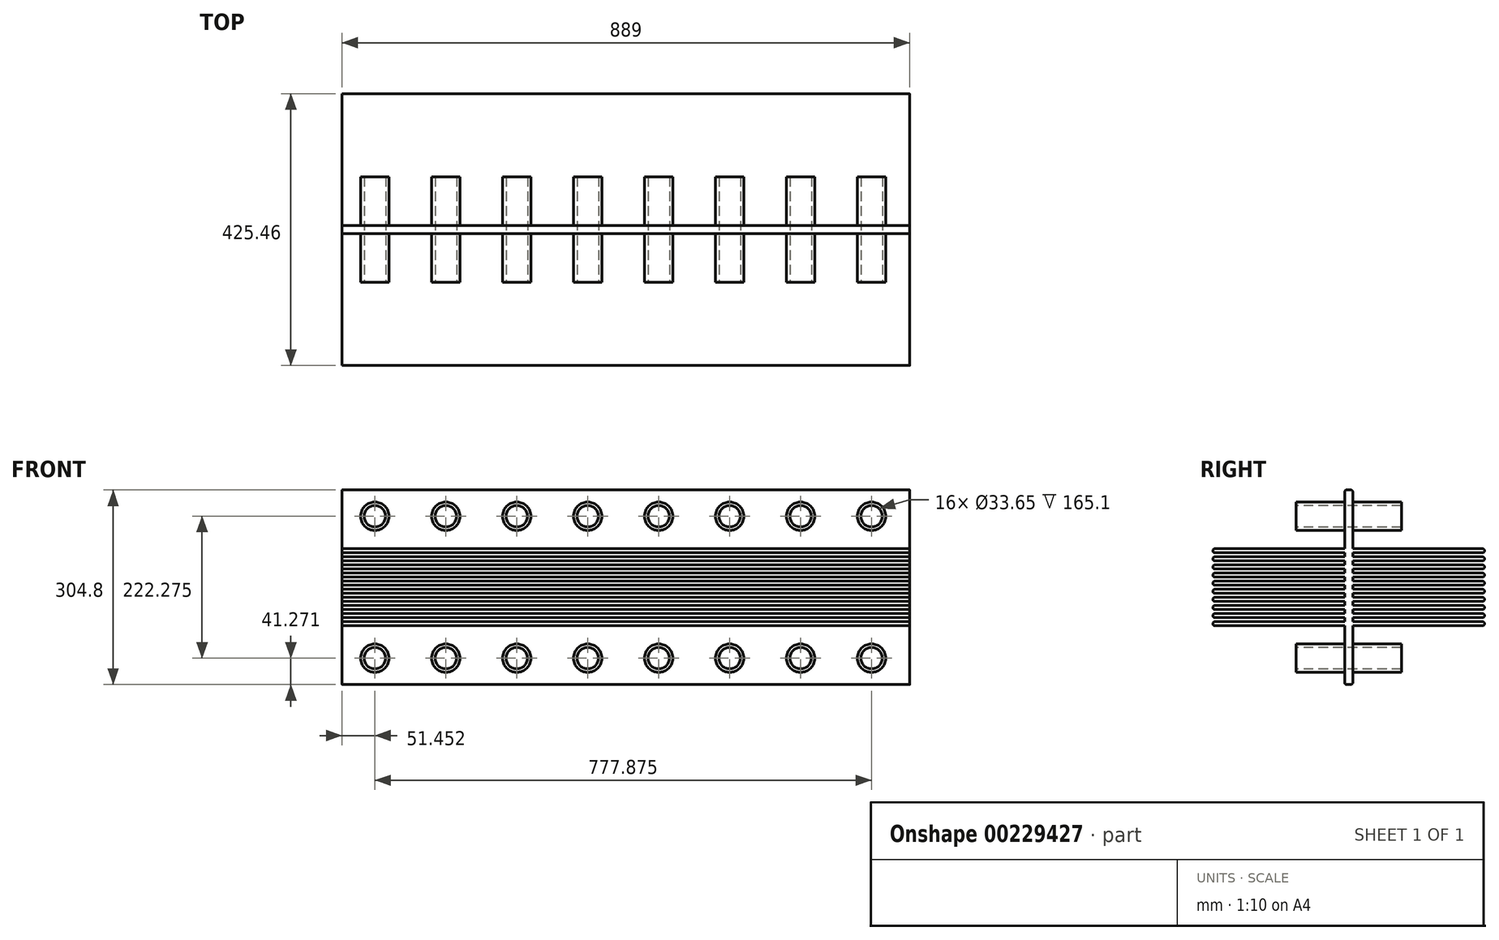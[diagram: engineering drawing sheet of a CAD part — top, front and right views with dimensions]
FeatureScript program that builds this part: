
annotation { "Feature Type Name" : "Feature", "Feature Type Description" : "" }
export const myFeature = defineFeature(function(context is Context, id is Id, definition is map)
    precondition{}
    {
        {
            var Q0;
            Q0=qCreatedBy(makeId("Front.planeOp"),FACE);
            var sketch = newSketch(context, id + "F0", { "sketchPlane" : qUnion([Q0])});
            skLineSegment(sketch, "E0.bottom", {"start": v(-439.22, 173.35) * mm, "end": v(449.78, 173.35) * mm});
            skLineSegment(sketch, "E0.top", {"start": v(-439.22, -131.45) * mm, "end": v(449.78, -131.45) * mm});
            skLineSegment(sketch, "E0.left", {"start": v(-439.22, 173.35) * mm, "end": v(-439.22, -131.45) * mm});
            skLineSegment(sketch, "E0.right", {"start": v(449.78, 173.35) * mm, "end": v(449.78, -131.45) * mm});
            skSolve(sketch);
        }
        {
            var Q0;
            Q0=makeQuery(id+"F0.imprint","IMPRINT",FACE,{"disambiguationData":[TD([[makeQuery(id+"F0.imprint","IMPRINT",EDGE,{"derivedFrom":sQuery(id+"F0.wireOp",EDGE,"E0.bottom")}),-1.0]])]});
            extrude(context, id + "F1", {"entities" : qUnion([Q0]), "depth" : 12.7 * mm});
        }
        {
            var Q0;
            Q0=makeQuery(id+"F1.opExtrude","CAP_FACE",FACE,{"disambiguationData":[OSD([sQuery(id+"F0.wireOp",EDGE,"E0.bottom"),sQuery(id+"F0.wireOp",EDGE,"E0.top"),sQuery(id+"F0.wireOp",EDGE,"E0.left"),sQuery(id+"F0.wireOp",EDGE,"E0.right")])],"isStart":false});
            var sketch = newSketch(context, id + "F2", { "sketchPlane" : qUnion([Q0])});
            skPoint(sketch, "E1", {"position": v(-387.77, -90.18) * mm});
            skPoint(sketch, "E2.0.1.0", {"position": v(-387.77, 132.1) * mm});
            skPoint(sketch, "E2.1.0.0", {"position": v(-276.64, -90.18) * mm});
            skPoint(sketch, "E2.1.1.0", {"position": v(-276.64, 132.1) * mm});
            skPoint(sketch, "E2.2.0.0", {"position": v(-165.52, -90.18) * mm});
            skPoint(sketch, "E2.2.1.0", {"position": v(-165.52, 132.1) * mm});
            skPoint(sketch, "E2.3.0.0", {"position": v(-54.4, -90.18) * mm});
            skPoint(sketch, "E2.3.1.0", {"position": v(-54.4, 132.1) * mm});
            skPoint(sketch, "E2.4.0.0", {"position": v(56.73, -90.18) * mm});
            skPoint(sketch, "E2.4.1.0", {"position": v(56.73, 132.1) * mm});
            skPoint(sketch, "E2.5.0.0", {"position": v(167.86, -90.18) * mm});
            skPoint(sketch, "E2.5.1.0", {"position": v(167.86, 132.1) * mm});
            skPoint(sketch, "E2.6.0.0", {"position": v(278.98, -90.18) * mm});
            skPoint(sketch, "E2.6.1.0", {"position": v(278.98, 132.1) * mm});
            skPoint(sketch, "E2.7.0.0", {"position": v(390.1, -90.18) * mm});
            skPoint(sketch, "E2.7.1.0", {"position": v(390.1, 132.1) * mm});
            skLineSegment(sketch, "E2.direction1", {"start": v(-387.77, -90.18) * mm, "end": v(-276.64, -90.18) * mm, "construction": true});
            skLineSegment(sketch, "E2.direction2", {"start": v(-387.77, -90.18) * mm, "end": v(-387.77, 132.1) * mm, "construction": true});
            skSolve(sketch);
        }
        {
            var Q0;
            Q0=makeQuery(id+"F1.opExtrude","SWEPT_FACE",FACE,{"disambiguationData":[OSD([sQuery(id+"F0.wireOp",EDGE,"E0.left")])]});
            var sketch = newSketch(context, id + "F3", { "sketchPlane" : qUnion([Q0])});
            skLineSegment(sketch, "E3", {"start": v(6.35, 173.35) * mm, "end": v(6.35, -131.45) * mm, "construction": true});
            skLineSegment(sketch, "E4", {"start": v(0, 20.95) * mm, "end": v(-70.4, 20.95) * mm, "construction": true});
            skPoint(sketch, "E4.endSnap0", {"position": v(0, 20.95) * mm});
            skLineSegment(sketch, "E5.MirrorCS", {"start": v(0, 24.12) * mm, "end": v(-203.2, 24.12) * mm});
            skLineSegment(sketch, "E6", {"start": v(0, 30.47) * mm, "end": v(-203.2, 30.47) * mm});
            skLineSegment(sketch, "E7", {"start": v(-203.2, 36.82) * mm, "end": v(0, 36.82) * mm});
            skLineSegment(sketch, "E8", {"start": v(-203.2, 43.17) * mm, "end": v(0, 43.17) * mm});
            skLineSegment(sketch, "E9", {"start": v(-203.2, 49.52) * mm, "end": v(0, 49.52) * mm});
            skLineSegment(sketch, "E10", {"start": v(-203.2, 55.87) * mm, "end": v(0, 55.87) * mm});
            skLineSegment(sketch, "E11", {"start": v(-203.2, 62.22) * mm, "end": v(0, 62.22) * mm});
            skLineSegment(sketch, "E12", {"start": v(-203.2, 68.57) * mm, "end": v(0, 68.57) * mm});
            skLineSegment(sketch, "E13", {"start": v(-203.2, 74.92) * mm, "end": v(0, 74.92) * mm});
            skLineSegment(sketch, "E14", {"start": v(-203.2, 81.27) * mm, "end": v(0, 81.27) * mm});
            skLineSegment(sketch, "E15.MirrorCS", {"start": v(12.7, 24.12) * mm, "end": v(215.9, 24.12) * mm});
            skLineSegment(sketch, "E16.MirrorCS", {"start": v(12.7, 30.47) * mm, "end": v(215.9, 30.47) * mm});
            skLineSegment(sketch, "E17.MirrorCS", {"start": v(215.9, 36.82) * mm, "end": v(12.7, 36.82) * mm});
            skLineSegment(sketch, "E18.MirrorCS", {"start": v(215.9, 43.17) * mm, "end": v(12.7, 43.17) * mm});
            skLineSegment(sketch, "E19.MirrorCS", {"start": v(215.9, 49.52) * mm, "end": v(12.7, 49.52) * mm});
            skLineSegment(sketch, "E20.MirrorCS", {"start": v(215.9, 55.87) * mm, "end": v(12.7, 55.87) * mm});
            skLineSegment(sketch, "E21.MirrorCS", {"start": v(215.9, 62.22) * mm, "end": v(12.7, 62.22) * mm});
            skLineSegment(sketch, "E22.MirrorCS", {"start": v(215.9, 68.57) * mm, "end": v(12.7, 68.57) * mm});
            skLineSegment(sketch, "E23.MirrorCS", {"start": v(215.9, 74.92) * mm, "end": v(12.7, 74.92) * mm});
            skLineSegment(sketch, "E24.MirrorCS", {"start": v(215.9, 81.27) * mm, "end": v(12.7, 81.27) * mm});
            skLineSegment(sketch, "E25.MirrorCS", {"start": v(0, 17.77) * mm, "end": v(-203.2, 17.77) * mm});
            skLineSegment(sketch, "E26.MirrorCS", {"start": v(0, 11.42) * mm, "end": v(-203.2, 11.42) * mm});
            skLineSegment(sketch, "E27.MirrorCS", {"start": v(-203.2, 5.07) * mm, "end": v(0, 5.07) * mm});
            skLineSegment(sketch, "E28.MirrorCS", {"start": v(-203.2, -1.28) * mm, "end": v(0, -1.28) * mm});
            skLineSegment(sketch, "E29.MirrorCS", {"start": v(-203.2, -7.63) * mm, "end": v(0, -7.63) * mm});
            skLineSegment(sketch, "E30.MirrorCS", {"start": v(-203.2, -13.98) * mm, "end": v(0, -13.98) * mm});
            skLineSegment(sketch, "E31.MirrorCS", {"start": v(-203.2, -20.33) * mm, "end": v(0, -20.33) * mm});
            skLineSegment(sketch, "E32.MirrorCS", {"start": v(-203.2, -26.68) * mm, "end": v(0, -26.68) * mm});
            skLineSegment(sketch, "E33.MirrorCS", {"start": v(-203.2, -33.03) * mm, "end": v(0, -33.03) * mm});
            skLineSegment(sketch, "E34.MirrorCS", {"start": v(-203.2, -39.38) * mm, "end": v(0, -39.38) * mm});
            skLineSegment(sketch, "E35.MirrorCS", {"start": v(215.9, -39.38) * mm, "end": v(12.7, -39.38) * mm});
            skLineSegment(sketch, "E36.MirrorCS", {"start": v(215.9, -33.03) * mm, "end": v(12.7, -33.03) * mm});
            skLineSegment(sketch, "E37.MirrorCS", {"start": v(215.9, -26.68) * mm, "end": v(12.7, -26.68) * mm});
            skLineSegment(sketch, "E38.MirrorCS", {"start": v(215.9, -20.33) * mm, "end": v(12.7, -20.33) * mm});
            skLineSegment(sketch, "E39.MirrorCS", {"start": v(215.9, -13.98) * mm, "end": v(12.7, -13.98) * mm});
            skLineSegment(sketch, "E40.MirrorCS", {"start": v(215.9, -7.63) * mm, "end": v(12.7, -7.63) * mm});
            skLineSegment(sketch, "E41.MirrorCS", {"start": v(215.9, -1.28) * mm, "end": v(12.7, -1.28) * mm});
            skLineSegment(sketch, "E42.MirrorCS", {"start": v(215.9, 5.07) * mm, "end": v(12.7, 5.07) * mm});
            skLineSegment(sketch, "E43.MirrorCS", {"start": v(12.7, 11.42) * mm, "end": v(215.9, 11.42) * mm});
            skLineSegment(sketch, "E44.MirrorCS", {"start": v(12.7, 17.77) * mm, "end": v(215.9, 17.77) * mm});
            skArc(sketch, "E45", {"start": v(-203.2, -33.03) * mm, "mid": v(-206.38, -36.2) * mm, "end": v(-203.2, -39.38) * mm});
            skArc(sketch, "E46", {"start": v(-203.2, -20.33) * mm, "mid": v(-206.37, -23.5) * mm, "end": v(-203.2, -26.68) * mm});
            skArc(sketch, "E47", {"start": v(-203.2, -7.63) * mm, "mid": v(-206.38, -10.8) * mm, "end": v(-203.2, -13.98) * mm});
            skArc(sketch, "E48", {"start": v(-203.2, 5.07) * mm, "mid": v(-206.38, 1.9) * mm, "end": v(-203.2, -1.28) * mm});
            skArc(sketch, "E49", {"start": v(-203.2, 17.77) * mm, "mid": v(-206.38, 14.6) * mm, "end": v(-203.2, 11.42) * mm});
            skArc(sketch, "E50", {"start": v(-203.2, 30.47) * mm, "mid": v(-206.38, 27.3) * mm, "end": v(-203.2, 24.12) * mm});
            skArc(sketch, "E51", {"start": v(-203.2, 43.17) * mm, "mid": v(-206.38, 40) * mm, "end": v(-203.2, 36.82) * mm});
            skArc(sketch, "E52", {"start": v(-203.2, 55.87) * mm, "mid": v(-206.38, 52.7) * mm, "end": v(-203.2, 49.52) * mm});
            skArc(sketch, "E53", {"start": v(-203.2, 68.57) * mm, "mid": v(-206.38, 65.4) * mm, "end": v(-203.2, 62.22) * mm});
            skArc(sketch, "E54", {"start": v(-203.2, 81.27) * mm, "mid": v(-206.38, 78.1) * mm, "end": v(-203.2, 74.92) * mm});
            skArc(sketch, "E55.MirrorCS", {"start": v(215.9, 81.27) * mm, "mid": v(219.08, 78.1) * mm, "end": v(215.9, 74.92) * mm});
            skArc(sketch, "E56.MirrorCS", {"start": v(215.9, 68.57) * mm, "mid": v(219.08, 65.4) * mm, "end": v(215.9, 62.22) * mm});
            skArc(sketch, "E57.MirrorCS", {"start": v(215.9, 55.87) * mm, "mid": v(219.08, 52.7) * mm, "end": v(215.9, 49.52) * mm});
            skArc(sketch, "E58.MirrorCS", {"start": v(215.9, 43.17) * mm, "mid": v(219.08, 40) * mm, "end": v(215.9, 36.82) * mm});
            skArc(sketch, "E59.MirrorCS", {"start": v(215.9, 30.47) * mm, "mid": v(219.08, 27.3) * mm, "end": v(215.9, 24.12) * mm});
            skArc(sketch, "E60.MirrorCS", {"start": v(215.9, 17.77) * mm, "mid": v(219.08, 14.6) * mm, "end": v(215.9, 11.42) * mm});
            skArc(sketch, "E61.MirrorCS", {"start": v(215.9, 5.07) * mm, "mid": v(219.08, 1.9) * mm, "end": v(215.9, -1.28) * mm});
            skArc(sketch, "E62.MirrorCS", {"start": v(215.9, -7.63) * mm, "mid": v(219.08, -10.8) * mm, "end": v(215.9, -13.98) * mm});
            skArc(sketch, "E63.MirrorCS", {"start": v(215.9, -20.33) * mm, "mid": v(219.07, -23.5) * mm, "end": v(215.9, -26.68) * mm});
            skArc(sketch, "E64.MirrorCS", {"start": v(215.9, -33.03) * mm, "mid": v(219.08, -36.2) * mm, "end": v(215.9, -39.38) * mm});
            skLineSegment(sketch, "E65", {"start": v(0, 81.27) * mm, "end": v(6.35, 81.27) * mm});
            skLineSegment(sketch, "E66", {"start": v(6.35, 81.27) * mm, "end": v(12.7, 81.27) * mm});
            skLineSegment(sketch, "E67", {"start": v(0, -39.38) * mm, "end": v(6.35, -39.38) * mm});
            skLineSegment(sketch, "E68", {"start": v(6.35, -39.38) * mm, "end": v(12.7, -39.38) * mm});
            skSolve(sketch);
        }
        {
            var Q0;
            Q0=makeQuery(id+"F1.opExtrude","SWEPT_FACE",FACE,{"disambiguationData":[OSD([sQuery(id+"F0.wireOp",EDGE,"E0.left")])]});
            var Q1;
            {var subQ0=sQuery(id+"F3.wireOp",EDGE,"E33.MirrorCS");Q1=makeQuery(id+"F3.imprint","IMPRINT",FACE,{"disambiguationData":[TD([[makeQuery(id+"F3.imprint","IMPRINT",EDGE,{"derivedFrom":subQ0}),-1.0]])]});}
            var Q2;
            {var subQ0=sQuery(id+"F3.wireOp",EDGE,"E31.MirrorCS");Q2=makeQuery(id+"F3.imprint","IMPRINT",FACE,{"disambiguationData":[TD([[makeQuery(id+"F3.imprint","IMPRINT",EDGE,{"derivedFrom":subQ0}),-1.0]])]});}
            var Q3;
            {var subQ0=sQuery(id+"F3.wireOp",EDGE,"E29.MirrorCS");Q3=makeQuery(id+"F3.imprint","IMPRINT",FACE,{"disambiguationData":[TD([[makeQuery(id+"F3.imprint","IMPRINT",EDGE,{"derivedFrom":subQ0}),-1.0]])]});}
            var Q4;
            {var subQ0=sQuery(id+"F3.wireOp",EDGE,"E27.MirrorCS");Q4=makeQuery(id+"F3.imprint","IMPRINT",FACE,{"disambiguationData":[TD([[makeQuery(id+"F3.imprint","IMPRINT",EDGE,{"derivedFrom":subQ0}),-1.0]])]});}
            var Q5;
            {var subQ0=sQuery(id+"F3.wireOp",EDGE,"E25.MirrorCS");Q5=makeQuery(id+"F3.imprint","IMPRINT",FACE,{"disambiguationData":[TD([[makeQuery(id+"F3.imprint","IMPRINT",EDGE,{"derivedFrom":subQ0}),1.0]])]});}
            var Q6;
            {var subQ0=sQuery(id+"F3.wireOp",EDGE,"E5.MirrorCS");Q6=makeQuery(id+"F3.imprint","IMPRINT",FACE,{"disambiguationData":[TD([[makeQuery(id+"F3.imprint","IMPRINT",EDGE,{"derivedFrom":subQ0}),-1.0]])]});}
            var Q7;
            {var subQ0=sQuery(id+"F3.wireOp",EDGE,"E7");Q7=makeQuery(id+"F3.imprint","IMPRINT",FACE,{"disambiguationData":[TD([[makeQuery(id+"F3.imprint","IMPRINT",EDGE,{"derivedFrom":subQ0}),1.0]])]});}
            var Q8;
            {var subQ0=sQuery(id+"F3.wireOp",EDGE,"E9");Q8=makeQuery(id+"F3.imprint","IMPRINT",FACE,{"disambiguationData":[TD([[makeQuery(id+"F3.imprint","IMPRINT",EDGE,{"derivedFrom":subQ0}),1.0]])]});}
            var Q9;
            {var subQ0=sQuery(id+"F3.wireOp",EDGE,"E11");Q9=makeQuery(id+"F3.imprint","IMPRINT",FACE,{"disambiguationData":[TD([[makeQuery(id+"F3.imprint","IMPRINT",EDGE,{"derivedFrom":subQ0}),1.0]])]});}
            var Q10;
            {var subQ0=sQuery(id+"F3.wireOp",EDGE,"E13");Q10=makeQuery(id+"F3.imprint","IMPRINT",FACE,{"disambiguationData":[TD([[makeQuery(id+"F3.imprint","IMPRINT",EDGE,{"derivedFrom":subQ0}),1.0]])]});}
            var Q11;
            {var subQ0=sQuery(id+"F3.wireOp",EDGE,"E35.MirrorCS");Q11=makeQuery(id+"F3.imprint","IMPRINT",FACE,{"disambiguationData":[TD([[makeQuery(id+"F3.imprint","IMPRINT",EDGE,{"derivedFrom":subQ0}),-1.0]])]});}
            var Q12;
            {var subQ0=sQuery(id+"F3.wireOp",EDGE,"E37.MirrorCS");Q12=makeQuery(id+"F3.imprint","IMPRINT",FACE,{"disambiguationData":[TD([[makeQuery(id+"F3.imprint","IMPRINT",EDGE,{"derivedFrom":subQ0}),-1.0]])]});}
            var Q13;
            {var subQ0=sQuery(id+"F3.wireOp",EDGE,"E39.MirrorCS");Q13=makeQuery(id+"F3.imprint","IMPRINT",FACE,{"disambiguationData":[TD([[makeQuery(id+"F3.imprint","IMPRINT",EDGE,{"derivedFrom":subQ0}),-1.0]])]});}
            var Q14;
            {var subQ0=sQuery(id+"F3.wireOp",EDGE,"E41.MirrorCS");Q14=makeQuery(id+"F3.imprint","IMPRINT",FACE,{"disambiguationData":[TD([[makeQuery(id+"F3.imprint","IMPRINT",EDGE,{"derivedFrom":subQ0}),-1.0]])]});}
            var Q15;
            {var subQ0=sQuery(id+"F3.wireOp",EDGE,"E43.MirrorCS");Q15=makeQuery(id+"F3.imprint","IMPRINT",FACE,{"disambiguationData":[TD([[makeQuery(id+"F3.imprint","IMPRINT",EDGE,{"derivedFrom":subQ0}),1.0]])]});}
            var Q16;
            {var subQ0=sQuery(id+"F3.wireOp",EDGE,"E15.MirrorCS");Q16=makeQuery(id+"F3.imprint","IMPRINT",FACE,{"disambiguationData":[TD([[makeQuery(id+"F3.imprint","IMPRINT",EDGE,{"derivedFrom":subQ0}),1.0]])]});}
            var Q17;
            {var subQ0=sQuery(id+"F3.wireOp",EDGE,"E17.MirrorCS");Q17=makeQuery(id+"F3.imprint","IMPRINT",FACE,{"disambiguationData":[TD([[makeQuery(id+"F3.imprint","IMPRINT",EDGE,{"derivedFrom":subQ0}),-1.0]])]});}
            var Q18;
            {var subQ0=sQuery(id+"F3.wireOp",EDGE,"E19.MirrorCS");Q18=makeQuery(id+"F3.imprint","IMPRINT",FACE,{"disambiguationData":[TD([[makeQuery(id+"F3.imprint","IMPRINT",EDGE,{"derivedFrom":subQ0}),-1.0]])]});}
            var Q19;
            {var subQ0=sQuery(id+"F3.wireOp",EDGE,"E21.MirrorCS");Q19=makeQuery(id+"F3.imprint","IMPRINT",FACE,{"disambiguationData":[TD([[makeQuery(id+"F3.imprint","IMPRINT",EDGE,{"derivedFrom":subQ0}),-1.0]])]});}
            var Q20;
            {var subQ0=sQuery(id+"F3.wireOp",EDGE,"E23.MirrorCS");Q20=makeQuery(id+"F3.imprint","IMPRINT",FACE,{"disambiguationData":[TD([[makeQuery(id+"F3.imprint","IMPRINT",EDGE,{"derivedFrom":subQ0}),-1.0]])]});}
            var Q21;
            Q21=makeQuery(id+"F1.opExtrude","SWEPT_FACE",FACE,{"disambiguationData":[OSD([sQuery(id+"F0.wireOp",EDGE,"E0.right")])]});
            extrude(context, id + "F4", {"entities" : qUnion([Q0, Q1, Q2, Q3, Q4, Q5, Q6, Q7, Q8, Q9, Q10, Q11, Q12, Q13, Q14, Q15, Q16, Q17, Q18, Q19, Q20]), "operationType" : NewBodyOperationType.ADD, "endBound" : BoundingType.UP_TO_SURFACE, "oppositeDirection" : true, "endBoundEntityFace" : qUnion([Q21]), "depth" : 25.4 * mm});
        }
        {
            var Q0;
            Q0=makeQuery(id+"F1.opExtrude","CAP_EDGE",EDGE,{"disambiguationData":[OSD([sQuery(id+"F0.wireOp",EDGE,"E0.bottom")])],"isStart":false});
            var Q1;
            Q1=makeQuery(id+"F1.opExtrude","CAP_EDGE",EDGE,{"disambiguationData":[OSD([sQuery(id+"F0.wireOp",EDGE,"E0.bottom")])],"isStart":true});
            var Q2;
            Q2=makeQuery(id+"F1.opExtrude","CAP_EDGE",EDGE,{"disambiguationData":[OSD([sQuery(id+"F0.wireOp",EDGE,"E0.top")])],"isStart":false});
            var Q3;
            Q3=makeQuery(id+"F1.opExtrude","CAP_EDGE",EDGE,{"disambiguationData":[OSD([sQuery(id+"F0.wireOp",EDGE,"E0.top")])],"isStart":true});
            fillet(context, id + "F5", {"entities" : qUnion([Q0, Q1, Q2, Q3]), "radius" : 3.17 * mm, "tangentPropagation" : true, "allowEdgeOverflow" : false});
        }
        {
            var Q0;
            Q0=sQuery(id+"F2.wireOp",VERTEX,"E1");
            var Q1;
            Q1=sQuery(id+"F2.wireOp",VERTEX,"E2.1.0.0");
            var Q2;
            Q2=sQuery(id+"F2.wireOp",VERTEX,"E2.2.0.0");
            var Q3;
            Q3=sQuery(id+"F2.wireOp",VERTEX,"E2.3.0.0");
            var Q4;
            Q4=sQuery(id+"F2.wireOp",VERTEX,"E2.4.0.0");
            var Q5;
            Q5=sQuery(id+"F2.wireOp",VERTEX,"E2.5.0.0");
            var Q6;
            Q6=sQuery(id+"F2.wireOp",VERTEX,"E2.6.0.0");
            var Q7;
            Q7=sQuery(id+"F2.wireOp",VERTEX,"E2.5.1.0");
            var Q8;
            Q8=sQuery(id+"F2.wireOp",VERTEX,"E2.4.1.0");
            var Q9;
            Q9=sQuery(id+"F2.wireOp",VERTEX,"E2.3.1.0");
            var Q10;
            Q10=sQuery(id+"F2.wireOp",VERTEX,"E2.2.1.0");
            var Q11;
            Q11=sQuery(id+"F2.wireOp",VERTEX,"E2.1.1.0");
            var Q12;
            Q12=sQuery(id+"F2.wireOp",VERTEX,"E2.0.1.0");
            var Q13;
            Q13=sQuery(id+"F2.wireOp",VERTEX,"E2.7.0.0");
            var Q14;
            Q14=sQuery(id+"F2.wireOp",VERTEX,"E2.7.1.0");
            var Q15;
            Q15=sQuery(id+"F2.wireOp",VERTEX,"E2.6.1.0");
            var Q16;
            Q16=makeQuery(id+"F1.opExtrude","SWEPT_BODY",BODY,{"disambiguationData":[OSD([sQuery(id+"F0.wireOp",EDGE,"E0.bottom"),sQuery(id+"F0.wireOp",EDGE,"E0.top"),sQuery(id+"F0.wireOp",EDGE,"E0.left"),sQuery(id+"F0.wireOp",EDGE,"E0.right")])]});
            hole(context, id + "F6", {"style" : HoleStyle.SIMPLE, "endStyle" : HoleEndStyle.THROUGH, "holeDiameter" : 33.65 * mm, "locations" : qUnion([Q0, Q1, Q2, Q3, Q4, Q5, Q6, Q7, Q8, Q9, Q10, Q11, Q12, Q13, Q14, Q15]), "scope" : qUnion([Q16]), "isTappedThrough" : true});
        }
        {
            var Q0;
            {var subQ3=sQuery(id+"F0.wireOp",EDGE,"E0.left");var subQ16=sQuery(id+"F0.wireOp",EDGE,"E0.right");var subQ44=sQuery(id+"F0.wireOp",EDGE,"E0.top");Q0=makeQuery(id+"F4.boolean.opBoolean","SPLIT",FACE,{"disambiguationData":[TD([makeQuery(id+"F1.opExtrude","SWEPT_FACE",FACE,{"disambiguationData":[OSD([subQ44])]})])],"derivedFrom":makeQuery(id+"F1.opExtrude","CAP_FACE",FACE,{"disambiguationData":[OSD([sQuery(id+"F0.wireOp",EDGE,"E0.bottom"),subQ44,subQ3,subQ16])],"isStart":false})});}
            var sketch = newSketch(context, id + "F7", { "sketchPlane" : qUnion([Q0])});
            skCircle(sketch, "E69", {"center": v(-387.77, -90.18) * mm, "radius": 22.24 * mm});
            skCircle(sketch, "E70.1.0.0", {"center": v(-276.64, -90.18) * mm, "radius": 22.24 * mm});
            skCircle(sketch, "E70.2.0.0", {"center": v(-165.52, -90.18) * mm, "radius": 22.24 * mm});
            skCircle(sketch, "E70.3.0.0", {"center": v(-54.4, -90.18) * mm, "radius": 22.24 * mm});
            skCircle(sketch, "E70.4.0.0", {"center": v(56.73, -90.18) * mm, "radius": 22.24 * mm});
            skCircle(sketch, "E70.5.0.0", {"center": v(167.86, -90.18) * mm, "radius": 22.24 * mm});
            skCircle(sketch, "E70.6.0.0", {"center": v(278.98, -90.18) * mm, "radius": 22.24 * mm});
            skCircle(sketch, "E70.7.0.0", {"center": v(390.1, -90.18) * mm, "radius": 22.24 * mm});
            skLineSegment(sketch, "E70.direction1", {"start": v(-387.77, -90.18) * mm, "end": v(-276.64, -90.18) * mm, "construction": true});
            skSolve(sketch);
        }
        {
            var Q0;
            {var subQ3=sQuery(id+"F0.wireOp",EDGE,"E0.left");var subQ13=sQuery(id+"F0.wireOp",EDGE,"E0.right");var subQ44=sQuery(id+"F0.wireOp",EDGE,"E0.bottom");Q0=makeQuery(id+"F4.boolean.opBoolean","SPLIT",FACE,{"disambiguationData":[TD([makeQuery(id+"F1.opExtrude","SWEPT_FACE",FACE,{"disambiguationData":[OSD([subQ44])]})])],"derivedFrom":makeQuery(id+"F1.opExtrude","CAP_FACE",FACE,{"disambiguationData":[OSD([subQ44,sQuery(id+"F0.wireOp",EDGE,"E0.top"),subQ3,subQ13])],"isStart":false})});}
            var sketch = newSketch(context, id + "F8", { "sketchPlane" : qUnion([Q0])});
            skCircle(sketch, "E71", {"center": v(-387.77, 132.1) * mm, "radius": 22.24 * mm});
            skCircle(sketch, "E72.1.0.0", {"center": v(-276.64, 132.1) * mm, "radius": 22.24 * mm});
            skCircle(sketch, "E72.2.0.0", {"center": v(-165.52, 132.1) * mm, "radius": 22.24 * mm});
            skCircle(sketch, "E72.3.0.0", {"center": v(-54.4, 132.1) * mm, "radius": 22.24 * mm});
            skCircle(sketch, "E72.4.0.0", {"center": v(56.73, 132.1) * mm, "radius": 22.24 * mm});
            skCircle(sketch, "E72.5.0.0", {"center": v(167.86, 132.1) * mm, "radius": 22.24 * mm});
            skCircle(sketch, "E72.6.0.0", {"center": v(278.98, 132.1) * mm, "radius": 22.24 * mm});
            skCircle(sketch, "E72.7.0.0", {"center": v(390.1, 132.1) * mm, "radius": 22.24 * mm});
            skLineSegment(sketch, "E72.direction1", {"start": v(-387.77, 132.1) * mm, "end": v(-276.64, 132.1) * mm, "construction": true});
            skSolve(sketch);
        }
        {
            var Q0;
            Q0=makeQuery(id+"F8.imprint","IMPRINT",FACE,{"disambiguationData":[TD([[makeQuery(id+"F8.imprint","IMPRINT",EDGE,{"derivedFrom":sQuery(id+"F8.wireOp",EDGE,"E71")}),1.0]])]});
            var Q1;
            Q1=makeQuery(id+"F8.imprint","IMPRINT",FACE,{"disambiguationData":[TD([[makeQuery(id+"F8.imprint","IMPRINT",EDGE,{"derivedFrom":sQuery(id+"F8.wireOp",EDGE,"E72.1.0.0")}),1.0]])]});
            var Q2;
            Q2=makeQuery(id+"F8.imprint","IMPRINT",FACE,{"disambiguationData":[TD([[makeQuery(id+"F8.imprint","IMPRINT",EDGE,{"derivedFrom":sQuery(id+"F8.wireOp",EDGE,"E72.2.0.0")}),1.0]])]});
            var Q3;
            Q3=makeQuery(id+"F8.imprint","IMPRINT",FACE,{"disambiguationData":[TD([[makeQuery(id+"F8.imprint","IMPRINT",EDGE,{"derivedFrom":sQuery(id+"F8.wireOp",EDGE,"E72.3.0.0")}),1.0]])]});
            var Q4;
            Q4=makeQuery(id+"F8.imprint","IMPRINT",FACE,{"disambiguationData":[TD([[makeQuery(id+"F8.imprint","IMPRINT",EDGE,{"derivedFrom":sQuery(id+"F8.wireOp",EDGE,"E72.4.0.0")}),1.0]])]});
            var Q5;
            Q5=makeQuery(id+"F8.imprint","IMPRINT",FACE,{"disambiguationData":[TD([[makeQuery(id+"F8.imprint","IMPRINT",EDGE,{"derivedFrom":sQuery(id+"F8.wireOp",EDGE,"E72.5.0.0")}),1.0]])]});
            var Q6;
            Q6=makeQuery(id+"F8.imprint","IMPRINT",FACE,{"disambiguationData":[TD([[makeQuery(id+"F8.imprint","IMPRINT",EDGE,{"derivedFrom":sQuery(id+"F8.wireOp",EDGE,"E72.6.0.0")}),1.0]])]});
            var Q7;
            Q7=makeQuery(id+"F8.imprint","IMPRINT",FACE,{"disambiguationData":[TD([[makeQuery(id+"F8.imprint","IMPRINT",EDGE,{"derivedFrom":sQuery(id+"F8.wireOp",EDGE,"E72.7.0.0")}),1.0]])]});
            var Q8;
            Q8=makeQuery(id+"F7.imprint","IMPRINT",FACE,{"disambiguationData":[TD([[makeQuery(id+"F7.imprint","IMPRINT",EDGE,{"derivedFrom":sQuery(id+"F7.wireOp",EDGE,"E69")}),1.0]])]});
            var Q9;
            Q9=makeQuery(id+"F7.imprint","IMPRINT",FACE,{"disambiguationData":[TD([[makeQuery(id+"F7.imprint","IMPRINT",EDGE,{"derivedFrom":sQuery(id+"F7.wireOp",EDGE,"E70.1.0.0")}),1.0]])]});
            var Q10;
            Q10=makeQuery(id+"F7.imprint","IMPRINT",FACE,{"disambiguationData":[TD([[makeQuery(id+"F7.imprint","IMPRINT",EDGE,{"derivedFrom":sQuery(id+"F7.wireOp",EDGE,"E70.2.0.0")}),1.0]])]});
            var Q11;
            Q11=makeQuery(id+"F7.imprint","IMPRINT",FACE,{"disambiguationData":[TD([[makeQuery(id+"F7.imprint","IMPRINT",EDGE,{"derivedFrom":sQuery(id+"F7.wireOp",EDGE,"E70.3.0.0")}),1.0]])]});
            var Q12;
            Q12=makeQuery(id+"F7.imprint","IMPRINT",FACE,{"disambiguationData":[TD([[makeQuery(id+"F7.imprint","IMPRINT",EDGE,{"derivedFrom":sQuery(id+"F7.wireOp",EDGE,"E70.4.0.0")}),1.0]])]});
            var Q13;
            Q13=makeQuery(id+"F7.imprint","IMPRINT",FACE,{"disambiguationData":[TD([[makeQuery(id+"F7.imprint","IMPRINT",EDGE,{"derivedFrom":sQuery(id+"F7.wireOp",EDGE,"E70.5.0.0")}),1.0]])]});
            var Q14;
            Q14=makeQuery(id+"F7.imprint","IMPRINT",FACE,{"disambiguationData":[TD([[makeQuery(id+"F7.imprint","IMPRINT",EDGE,{"derivedFrom":sQuery(id+"F7.wireOp",EDGE,"E70.6.0.0")}),1.0]])]});
            var Q15;
            Q15=makeQuery(id+"F7.imprint","IMPRINT",FACE,{"disambiguationData":[TD([[makeQuery(id+"F7.imprint","IMPRINT",EDGE,{"derivedFrom":sQuery(id+"F7.wireOp",EDGE,"E70.7.0.0")}),1.0]])]});
            extrude(context, id + "F9", {"entities" : qUnion([Q0, Q1, Q2, Q3, Q4, Q5, Q6, Q7, Q8, Q9, Q10, Q11, Q12, Q13, Q14, Q15]), "operationType" : NewBodyOperationType.ADD, "depth" : 76.2 * mm});
        }
        {
            var Q0;
            {var subQ3=sQuery(id+"F0.wireOp",EDGE,"E0.left");var subQ13=sQuery(id+"F0.wireOp",EDGE,"E0.right");var subQ44=sQuery(id+"F0.wireOp",EDGE,"E0.bottom");Q0=makeQuery(id+"F4.boolean.opBoolean","SPLIT",FACE,{"disambiguationData":[TD([makeQuery(id+"F1.opExtrude","SWEPT_FACE",FACE,{"disambiguationData":[OSD([subQ44])]})])],"derivedFrom":makeQuery(id+"F1.opExtrude","CAP_FACE",FACE,{"disambiguationData":[OSD([subQ44,sQuery(id+"F0.wireOp",EDGE,"E0.top"),subQ3,subQ13])],"isStart":true})});}
            var sketch = newSketch(context, id + "F10", { "sketchPlane" : qUnion([Q0])});
            skCircle(sketch, "E73", {"center": v(-390.1, 132.1) * mm, "radius": 22.24 * mm});
            skCircle(sketch, "E74.1.0.0", {"center": v(-278.98, 132.1) * mm, "radius": 22.24 * mm});
            skCircle(sketch, "E74.2.0.0", {"center": v(-167.86, 132.1) * mm, "radius": 22.24 * mm});
            skCircle(sketch, "E74.3.0.0", {"center": v(-56.73, 132.1) * mm, "radius": 22.24 * mm});
            skCircle(sketch, "E74.4.0.0", {"center": v(54.4, 132.1) * mm, "radius": 22.24 * mm});
            skCircle(sketch, "E74.5.0.0", {"center": v(165.52, 132.1) * mm, "radius": 22.24 * mm});
            skCircle(sketch, "E74.6.0.0", {"center": v(276.64, 132.1) * mm, "radius": 22.24 * mm});
            skCircle(sketch, "E74.7.0.0", {"center": v(387.77, 132.1) * mm, "radius": 22.24 * mm});
            skLineSegment(sketch, "E74.direction1", {"start": v(-390.1, 132.1) * mm, "end": v(-278.98, 132.1) * mm, "construction": true});
            skSolve(sketch);
        }
        {
            var Q0;
            {var subQ3=sQuery(id+"F0.wireOp",EDGE,"E0.left");var subQ10=sQuery(id+"F0.wireOp",EDGE,"E0.right");var subQ44=sQuery(id+"F0.wireOp",EDGE,"E0.top");Q0=makeQuery(id+"F4.boolean.opBoolean","SPLIT",FACE,{"disambiguationData":[TD([makeQuery(id+"F1.opExtrude","SWEPT_FACE",FACE,{"disambiguationData":[OSD([subQ44])]})])],"derivedFrom":makeQuery(id+"F1.opExtrude","CAP_FACE",FACE,{"disambiguationData":[OSD([sQuery(id+"F0.wireOp",EDGE,"E0.bottom"),subQ44,subQ3,subQ10])],"isStart":true})});}
            var sketch = newSketch(context, id + "F11", { "sketchPlane" : qUnion([Q0])});
            skCircle(sketch, "E75", {"center": v(-390.1, -90.18) * mm, "radius": 22.24 * mm});
            skCircle(sketch, "E76.1.0.0", {"center": v(-278.98, -90.18) * mm, "radius": 22.24 * mm});
            skCircle(sketch, "E76.2.0.0", {"center": v(-167.86, -90.18) * mm, "radius": 22.24 * mm});
            skCircle(sketch, "E76.3.0.0", {"center": v(-56.73, -90.18) * mm, "radius": 22.24 * mm});
            skCircle(sketch, "E76.4.0.0", {"center": v(54.4, -90.18) * mm, "radius": 22.24 * mm});
            skCircle(sketch, "E76.5.0.0", {"center": v(165.52, -90.18) * mm, "radius": 22.24 * mm});
            skCircle(sketch, "E76.6.0.0", {"center": v(276.64, -90.18) * mm, "radius": 22.24 * mm});
            skCircle(sketch, "E76.7.0.0", {"center": v(387.77, -90.18) * mm, "radius": 22.24 * mm});
            skLineSegment(sketch, "E76.direction1", {"start": v(-390.1, -90.18) * mm, "end": v(-278.98, -90.18) * mm, "construction": true});
            skSolve(sketch);
        }
        {
            var Q0;
            Q0=makeQuery(id+"F10.imprint","IMPRINT",FACE,{"disambiguationData":[TD([[makeQuery(id+"F10.imprint","IMPRINT",EDGE,{"derivedFrom":sQuery(id+"F10.wireOp",EDGE,"E73")}),1.0]])]});
            var Q1;
            Q1=makeQuery(id+"F10.imprint","IMPRINT",FACE,{"disambiguationData":[TD([[makeQuery(id+"F10.imprint","IMPRINT",EDGE,{"derivedFrom":sQuery(id+"F10.wireOp",EDGE,"E74.1.0.0")}),1.0]])]});
            var Q2;
            Q2=makeQuery(id+"F10.imprint","IMPRINT",FACE,{"disambiguationData":[TD([[makeQuery(id+"F10.imprint","IMPRINT",EDGE,{"derivedFrom":sQuery(id+"F10.wireOp",EDGE,"E74.2.0.0")}),1.0]])]});
            var Q3;
            Q3=makeQuery(id+"F10.imprint","IMPRINT",FACE,{"disambiguationData":[TD([[makeQuery(id+"F10.imprint","IMPRINT",EDGE,{"derivedFrom":sQuery(id+"F10.wireOp",EDGE,"E74.3.0.0")}),1.0]])]});
            var Q4;
            Q4=makeQuery(id+"F10.imprint","IMPRINT",FACE,{"disambiguationData":[TD([[makeQuery(id+"F10.imprint","IMPRINT",EDGE,{"derivedFrom":sQuery(id+"F10.wireOp",EDGE,"E74.4.0.0")}),1.0]])]});
            var Q5;
            Q5=makeQuery(id+"F10.imprint","IMPRINT",FACE,{"disambiguationData":[TD([[makeQuery(id+"F10.imprint","IMPRINT",EDGE,{"derivedFrom":sQuery(id+"F10.wireOp",EDGE,"E74.5.0.0")}),1.0]])]});
            var Q6;
            Q6=makeQuery(id+"F10.imprint","IMPRINT",FACE,{"disambiguationData":[TD([[makeQuery(id+"F10.imprint","IMPRINT",EDGE,{"derivedFrom":sQuery(id+"F10.wireOp",EDGE,"E74.6.0.0")}),1.0]])]});
            var Q7;
            Q7=makeQuery(id+"F10.imprint","IMPRINT",FACE,{"disambiguationData":[TD([[makeQuery(id+"F10.imprint","IMPRINT",EDGE,{"derivedFrom":sQuery(id+"F10.wireOp",EDGE,"E74.7.0.0")}),1.0]])]});
            var Q8;
            Q8=makeQuery(id+"F11.imprint","IMPRINT",FACE,{"disambiguationData":[TD([[makeQuery(id+"F11.imprint","IMPRINT",EDGE,{"derivedFrom":sQuery(id+"F11.wireOp",EDGE,"E75")}),1.0]])]});
            var Q9;
            Q9=makeQuery(id+"F11.imprint","IMPRINT",FACE,{"disambiguationData":[TD([[makeQuery(id+"F11.imprint","IMPRINT",EDGE,{"derivedFrom":sQuery(id+"F11.wireOp",EDGE,"E76.1.0.0")}),1.0]])]});
            var Q10;
            Q10=makeQuery(id+"F11.imprint","IMPRINT",FACE,{"disambiguationData":[TD([[makeQuery(id+"F11.imprint","IMPRINT",EDGE,{"derivedFrom":sQuery(id+"F11.wireOp",EDGE,"E76.2.0.0")}),1.0]])]});
            var Q11;
            Q11=makeQuery(id+"F11.imprint","IMPRINT",FACE,{"disambiguationData":[TD([[makeQuery(id+"F11.imprint","IMPRINT",EDGE,{"derivedFrom":sQuery(id+"F11.wireOp",EDGE,"E76.3.0.0")}),1.0]])]});
            var Q12;
            Q12=makeQuery(id+"F11.imprint","IMPRINT",FACE,{"disambiguationData":[TD([[makeQuery(id+"F11.imprint","IMPRINT",EDGE,{"derivedFrom":sQuery(id+"F11.wireOp",EDGE,"E76.4.0.0")}),1.0]])]});
            var Q13;
            Q13=makeQuery(id+"F11.imprint","IMPRINT",FACE,{"disambiguationData":[TD([[makeQuery(id+"F11.imprint","IMPRINT",EDGE,{"derivedFrom":sQuery(id+"F11.wireOp",EDGE,"E76.5.0.0")}),1.0]])]});
            var Q14;
            Q14=makeQuery(id+"F11.imprint","IMPRINT",FACE,{"disambiguationData":[TD([[makeQuery(id+"F11.imprint","IMPRINT",EDGE,{"derivedFrom":sQuery(id+"F11.wireOp",EDGE,"E76.6.0.0")}),1.0]])]});
            var Q15;
            Q15=makeQuery(id+"F11.imprint","IMPRINT",FACE,{"disambiguationData":[TD([[makeQuery(id+"F11.imprint","IMPRINT",EDGE,{"derivedFrom":sQuery(id+"F11.wireOp",EDGE,"E76.7.0.0")}),1.0]])]});
            extrude(context, id + "F12", {"entities" : qUnion([Q0, Q1, Q2, Q3, Q4, Q5, Q6, Q7, Q8, Q9, Q10, Q11, Q12, Q13, Q14, Q15]), "operationType" : NewBodyOperationType.ADD, "depth" : 76.2 * mm});
        }
    });
